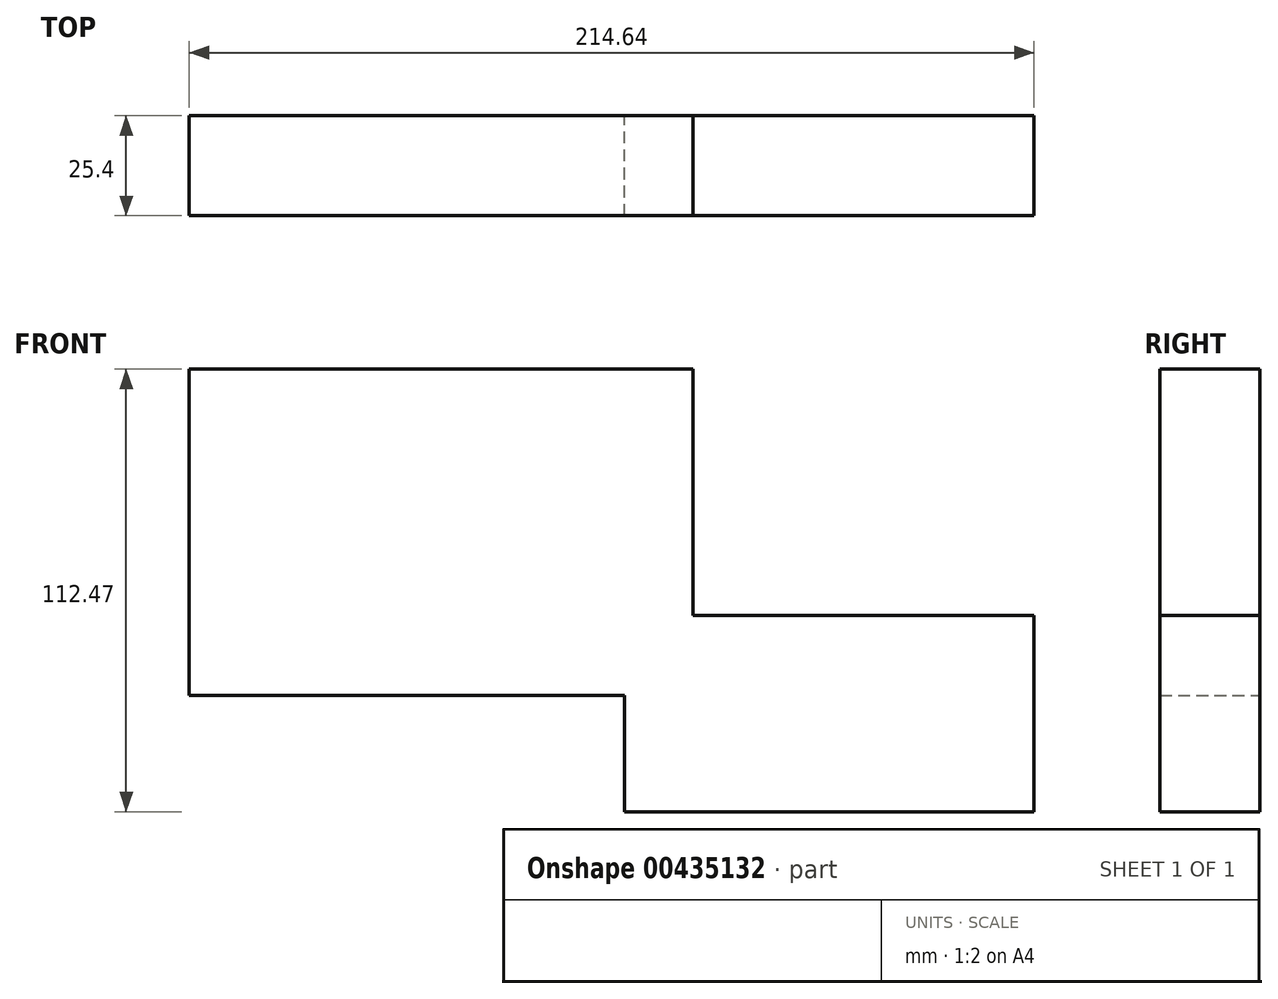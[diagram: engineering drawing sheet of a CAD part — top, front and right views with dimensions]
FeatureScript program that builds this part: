
annotation { "Feature Type Name" : "Feature", "Feature Type Description" : "" }
export const myFeature = defineFeature(function(context is Context, id is Id, definition is map)
    precondition{}
    {
        {
            var Q0;
            Q0=qCreatedBy(makeId("Front.planeOp"),FACE);
            var sketch = newSketch(context, id + "F0", { "sketchPlane" : qUnion([Q0])});
            skLineSegment(sketch, "E0.bottom", {"start": v(-52.7, 17.19) * mm, "end": v(51.37, 17.19) * mm});
            skLineSegment(sketch, "E0.top", {"start": v(-52.7, -32.65) * mm, "end": v(51.37, -32.65) * mm});
            skLineSegment(sketch, "E0.left", {"start": v(-52.7, 17.19) * mm, "end": v(-52.7, -32.65) * mm});
            skLineSegment(sketch, "E0.right", {"start": v(51.37, 17.19) * mm, "end": v(51.37, -32.65) * mm});
            skLineSegment(sketch, "E1.bottom", {"start": v(-35.33, -3.06) * mm, "end": v(-163.27, -3.06) * mm});
            skLineSegment(sketch, "E1.top", {"start": v(-35.33, 79.82) * mm, "end": v(-163.27, 79.82) * mm});
            skLineSegment(sketch, "E1.left", {"start": v(-35.33, -3.06) * mm, "end": v(-35.33, 79.82) * mm});
            skLineSegment(sketch, "E1.right", {"start": v(-163.27, -3.06) * mm, "end": v(-163.27, 79.82) * mm});
            skSolve(sketch);
        }
        {
            var Q0;
            Q0 = qSketchRegion(id + "F0", true);
            extrude(context, id + "F1", {"entities" : qUnion([Q0]), "depth" : 25.4 * mm});
        }
    });
